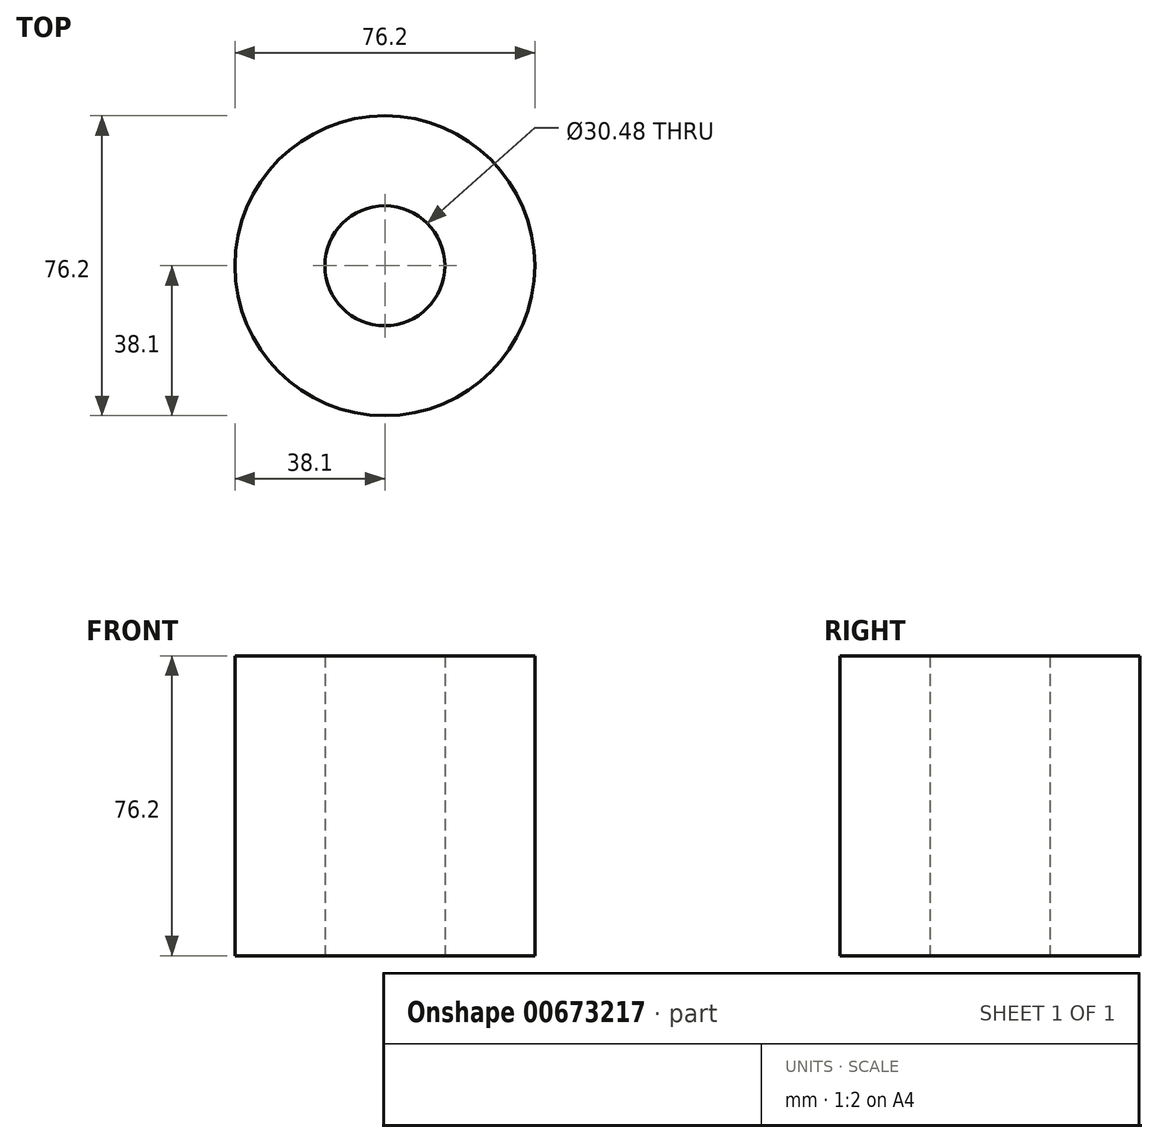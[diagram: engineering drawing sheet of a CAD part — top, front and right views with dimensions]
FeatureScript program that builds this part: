
annotation { "Feature Type Name" : "Feature", "Feature Type Description" : "" }
export const myFeature = defineFeature(function(context is Context, id is Id, definition is map)
    precondition{}
    {
        {
            var Q0;
            Q0=qCreatedBy(makeId("Top.planeOp"),FACE);
            var sketch = newSketch(context, id + "F0", { "sketchPlane" : qUnion([Q0])});
            skCircle(sketch, "E0", {"center": v(0, 0) * mm, "radius": 15.24 * mm});
            skCircle(sketch, "E1", {"center": v(0, 0) * mm, "radius": 38.1 * mm});
            skSolve(sketch);
        }
        {
            var Q0;
            Q0 = qSketchRegion(id + "F0", true);
            extrude(context, id + "F1", {"entities" : qUnion([Q0]), "depth" : 76.2 * mm, "offsetDistance" : 25.4 * mm});
        }
    });
